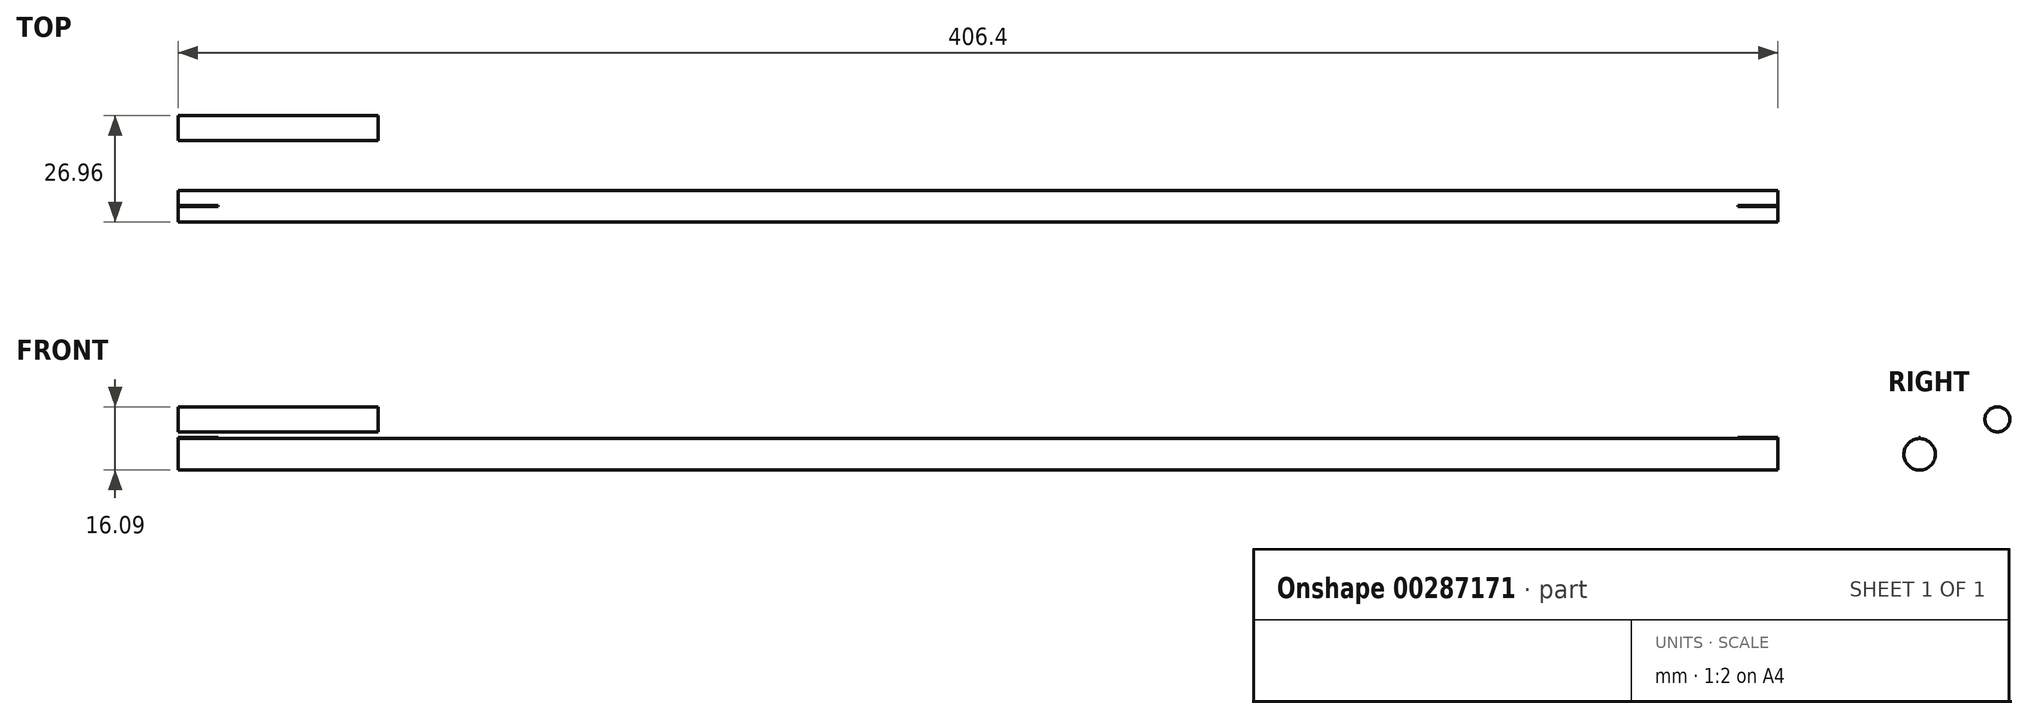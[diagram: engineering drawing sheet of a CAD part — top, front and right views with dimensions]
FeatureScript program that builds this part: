
annotation { "Feature Type Name" : "Feature", "Feature Type Description" : "" }
export const myFeature = defineFeature(function(context is Context, id is Id, definition is map)
    precondition{}
    {
        {
            var Q0;
            Q0=qCreatedBy(makeId("Right.planeOp"),FACE);
            var sketch = newSketch(context, id + "F0", { "sketchPlane" : qUnion([Q0])});
            skCircle(sketch, "E0", {"center": v(0, 0) * mm, "radius": 4 * mm});
            skSolve(sketch);
        }
        {
            var Q0;
            Q0=makeQuery(id+"F0.imprint","IMPRINT",FACE,{"disambiguationData":[TD([[makeQuery(id+"F0.imprint","IMPRINT",EDGE,{"derivedFrom":sQuery(id+"F0.wireOp",EDGE,"E0")}),1.0]])]});
            extrude(context, id + "F1", {"entities" : qUnion([Q0]), "depth" : 406.4 * mm});
        }
        {
            var Q0;
            Q0=makeQuery(id+"F1.opExtrude","CAP_FACE",FACE,{"disambiguationData":[OSD([sQuery(id+"F0.wireOp",EDGE,"E0")])],"isStart":false});
            cPlane(context, id + "F2", {"entities" : qUnion([Q0]), "cplaneType" : CPlaneType.OFFSET, "offset" : 25.4 * mm, "oppositeDirection" : true, "width" : 152.4 * mm, "height" : 152.4 * mm});
        }
        {
            var Q0;
            Q0=makeQuery(id+"F1.opExtrude","CAP_FACE",FACE,{"disambiguationData":[OSD([sQuery(id+"F0.wireOp",EDGE,"E0")])],"isStart":true});
            cPlane(context, id + "F3", {"entities" : qUnion([Q0]), "cplaneType" : CPlaneType.OFFSET, "offset" : 25.4 * mm, "oppositeDirection" : true, "width" : 152.4 * mm, "height" : 152.4 * mm});
        }
        {
            var Q0;
            Q0=qCreatedBy(id+"F3.planeOp",FACE);
            var sketch = newSketch(context, id + "F4", { "sketchPlane" : qUnion([Q0])});
            skPoint(sketch, "E1", {"position": v(0, 0) * mm});
            skSolve(sketch);
        }
        {
            var Q0;
            Q0=qCreatedBy(id+"F2.planeOp",FACE);
            var sketch = newSketch(context, id + "F5", { "sketchPlane" : qUnion([Q0])});
            skPoint(sketch, "E2", {"position": v(0, 0) * mm});
            skSolve(sketch);
        }
        {
            var Q0;
            Q0=makeQuery(id+"F1.opExtrude","CAP_FACE",FACE,{"disambiguationData":[OSD([sQuery(id+"F0.wireOp",EDGE,"E0")])],"isStart":false});
            var sketch = newSketch(context, id + "F6", { "sketchPlane" : qUnion([Q0])});
            skLineSegment(sketch, "E3.bottom", {"start": v(-0.16, 4) * mm, "end": v(0.15, 4) * mm});
            skLineSegment(sketch, "E3.top", {"start": v(-0.16, 4.3) * mm, "end": v(0.15, 4.3) * mm});
            skLineSegment(sketch, "E3.left", {"start": v(-0.16, 4) * mm, "end": v(-0.16, 4.3) * mm});
            skLineSegment(sketch, "E3.right", {"start": v(0.15, 4) * mm, "end": v(0.15, 4.3) * mm});
            skSolve(sketch);
        }
        {
            var Q0;
            Q0 = qSketchRegion(id + "F6", true);
            extrude(context, id + "F7", {"entities" : qUnion([Q0]), "operationType" : NewBodyOperationType.ADD, "oppositeDirection" : true, "depth" : 10.16 * mm});
        }
        {
            var Q0;
            Q0=makeQuery(id+"F1.opExtrude","CAP_FACE",FACE,{"disambiguationData":[OSD([sQuery(id+"F0.wireOp",EDGE,"E0")])],"isStart":true});
            var sketch = newSketch(context, id + "F8", { "sketchPlane" : qUnion([Q0])});
            skLineSegment(sketch, "E4.bottom", {"start": v(-0.15, 4) * mm, "end": v(0.15, 4) * mm});
            skLineSegment(sketch, "E4.top", {"start": v(-0.15, 4.3) * mm, "end": v(0.15, 4.3) * mm});
            skLineSegment(sketch, "E4.left", {"start": v(-0.15, 4) * mm, "end": v(-0.15, 4.3) * mm});
            skLineSegment(sketch, "E4.right", {"start": v(0.15, 4) * mm, "end": v(0.15, 4.3) * mm});
            skSolve(sketch);
        }
        {
            var Q0;
            Q0 = qSketchRegion(id + "F8", true);
            extrude(context, id + "F9", {"entities" : qUnion([Q0]), "operationType" : NewBodyOperationType.ADD, "oppositeDirection" : true, "depth" : 10.16 * mm});
        }
        {
            var Q0;
            Q0=qCreatedBy(makeId("Right.planeOp"),FACE);
            var sketch = newSketch(context, id + "F10", { "sketchPlane" : qUnion([Q0])});
            skLineSegment(sketch, "E5", {"start": v(19.78, 0) * mm, "end": v(19.78, 8.92) * mm, "construction": true});
            skLineSegment(sketch, "E6", {"start": v(19.78, 8.92) * mm, "end": v(29.48, 8.92) * mm, "construction": true});
            skCircle(sketch, "E7", {"center": v(19.78, 8.92) * mm, "radius": 3.18 * mm});
            skSolve(sketch);
        }
        {
            var Q0;
            Q0=makeQuery(id+"F10.imprint","IMPRINT",FACE,{"disambiguationData":[TD([[makeQuery(id+"F10.imprint","IMPRINT",EDGE,{"derivedFrom":sQuery(id+"F10.wireOp",EDGE,"E7")}),1.0]])]});
            extrude(context, id + "F11", {"entities" : qUnion([Q0]), "depth" : 50.8 * mm});
        }
    });
